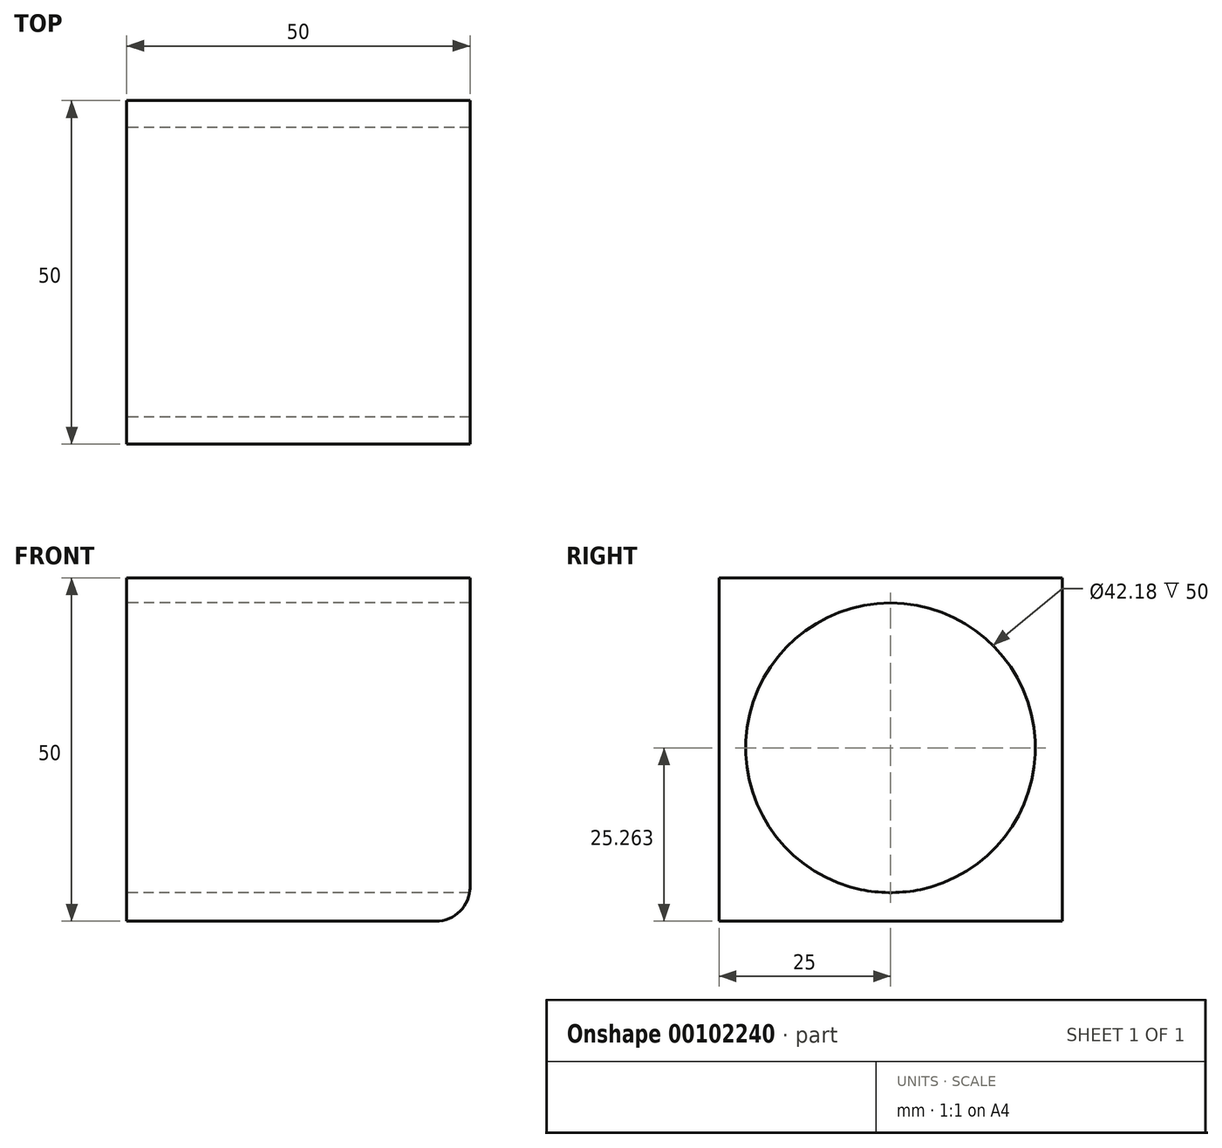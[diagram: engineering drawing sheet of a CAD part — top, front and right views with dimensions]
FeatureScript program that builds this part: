
annotation { "Feature Type Name" : "Feature", "Feature Type Description" : "" }
export const myFeature = defineFeature(function(context is Context, id is Id, definition is map)
    precondition{}
    {
        {
            var Q0;
            Q0=qCreatedBy(makeId("Top.planeOp"),FACE);
            var sketch = newSketch(context, id + "F0", { "sketchPlane" : qUnion([Q0])});
            skLineSegment(sketch, "E0.bottom", {"start": v(25, 25) * mm, "end": v(-25, 25) * mm});
            skLineSegment(sketch, "E0.top", {"start": v(25, -25) * mm, "end": v(-25, -25) * mm});
            skLineSegment(sketch, "E0.left", {"start": v(25, 25) * mm, "end": v(25, -25) * mm});
            skLineSegment(sketch, "E0.right", {"start": v(-25, 25) * mm, "end": v(-25, -25) * mm});
            skPoint(sketch, "E0.middle", {"position": v(0, 0) * mm});
            skSolve(sketch);
        }
        {
            var Q0;
            Q0 = qSketchRegion(id + "F0", true);
            extrude(context, id + "F1", {"entities" : qUnion([Q0]), "depth" : 50 * mm});
        }
        {
            var Q0;
            Q0=makeQuery(id+"F1.opExtrude","SWEPT_FACE",FACE,{"disambiguationData":[OSD([sQuery(id+"F0.wireOp",EDGE,"E0.right")])]});
            var sketch = newSketch(context, id + "F2", { "sketchPlane" : qUnion([Q0])});
            skCircle(sketch, "E1", {"center": v(0, 25.26) * mm, "radius": 21.09 * mm});
            skSolve(sketch);
        }
        {
            var Q0;
            Q0=makeQuery(id+"F2.imprint","IMPRINT",FACE,{"disambiguationData":[TD([[makeQuery(id+"F2.imprint","IMPRINT",EDGE,{"derivedFrom":sQuery(id+"F2.wireOp",EDGE,"E1")}),1.0]])]});
            extrude(context, id + "F4", {"entities" : qUnion([Q0]), "operationType" : NewBodyOperationType.REMOVE, "endBound" : BoundingType.THROUGH_ALL, "oppositeDirection" : true, "depth" : 25 * mm});
        }
        {
            var Q0;
            Q0=makeQuery(id+"F1.opExtrude","CAP_EDGE",EDGE,{"disambiguationData":[OSD([sQuery(id+"F0.wireOp",EDGE,"E0.left")])],"isStart":true});
            fillet(context, id + "F3", {"entities" : qUnion([Q0]), "radius" : 5 * mm, "tangentPropagation" : true, "allowEdgeOverflow" : false});
        }
    });
